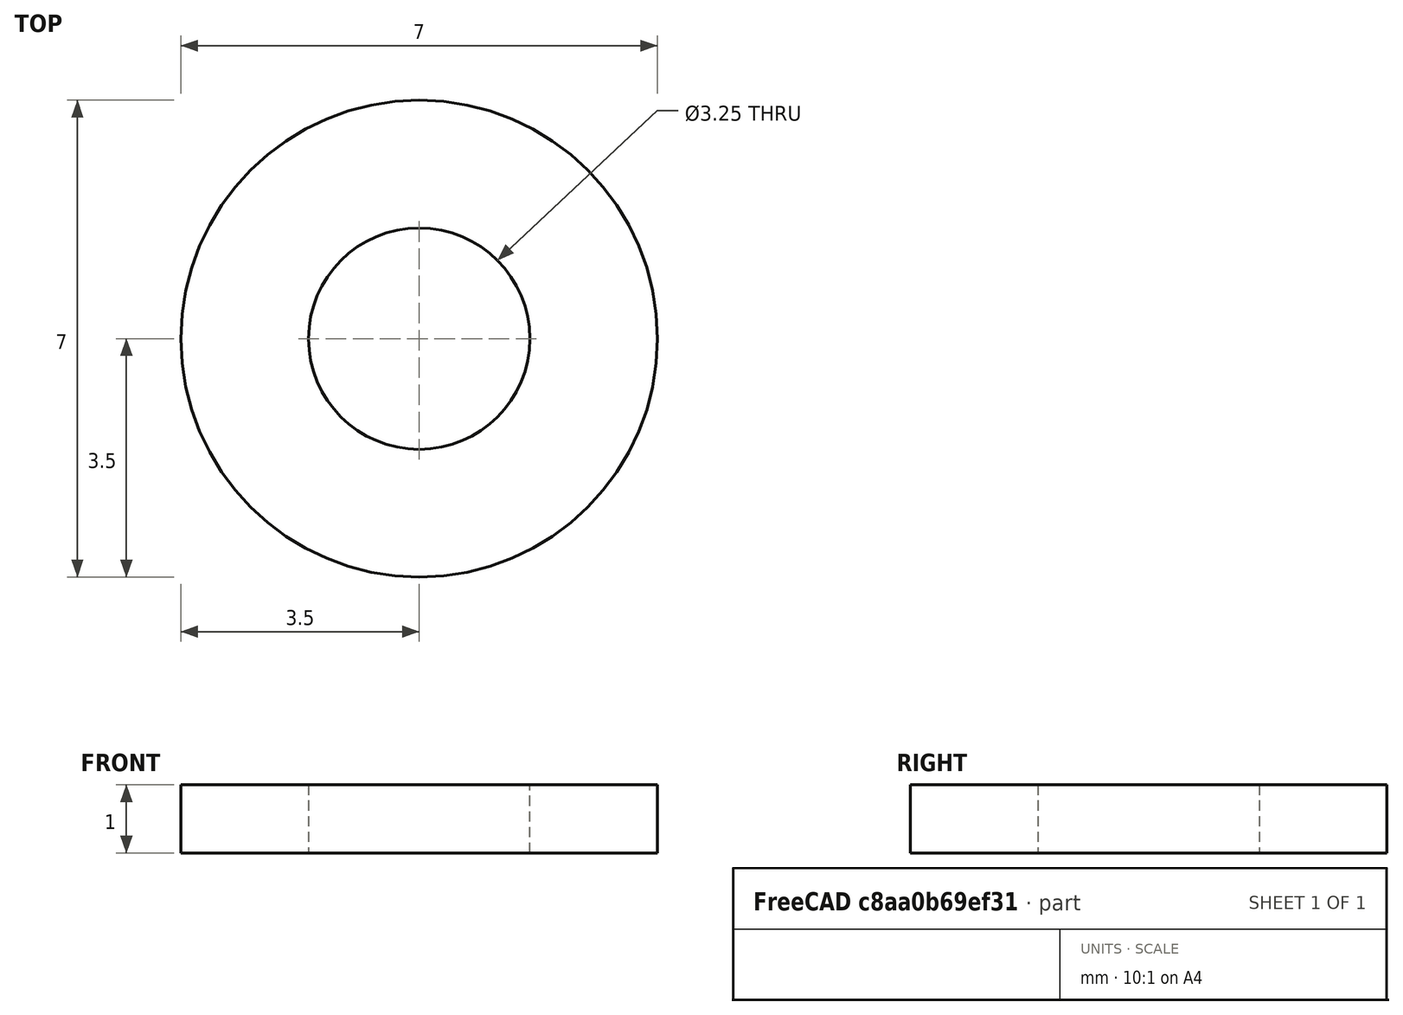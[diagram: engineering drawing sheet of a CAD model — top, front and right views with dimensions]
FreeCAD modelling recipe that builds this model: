
FCSTD DOCUMENT  (FreeCAD 1.1R40303 (Git))
Label: spacer
License: All rights reserved
LicenseURL: http://en.wikipedia.org/wiki/All_rights_reserved
objects: App::Point×1, Sketcher::SketchObject×1, PartDesign::Pad×1, PartDesign::Body×1
note: 6 computed .brp shape members not serialized (recipe doc carries the construction recipe); baked Part::Feature solids carry a one-line shape summary decoded from their .brp

FEATURE [App::Point] Origin001
  Role = Origin
FEATURE [Sketcher::SketchObject] Sketch
  ArcFitTolerance = 1e-06
  AttachmentSupport = -> [XY_Plane]
  ExternalTypes = [0]
  FullyConstrained = true
  MakeInternals = false
  MapMode = 5
  sketch-geometry (2):
    g0: Circle CenterX=0 CenterY=0 CenterZ=0 NormalX=0 NormalY=0 NormalZ=1 AngleXU=0 Radius=3.5
    g1: Circle CenterX=0 CenterY=0 CenterZ=0 NormalX=0 NormalY=0 NormalZ=1 AngleXU=0 Radius=1.625
  constraints (4):
    c: Coincident(g0,g-1)
    c: Diameter(g0) = 7
    c: Coincident(g1,g0)
    c: Diameter(g1) = 3.25
FEATURE [PartDesign::Pad] Pad
  Direction = (0,0,1)
  Length = 1
  Length2 = 10
  Profile = -> Sketch
  ReferenceAxis = -> Sketch [N_Axis]
  Suppressed = false
  Type = 0
FEATURE [PartDesign::Body] Body
  AllowCompound = false
  Group = -> [Sketch,Pad]
  Origin = -> Origin
  Tip = -> Pad
